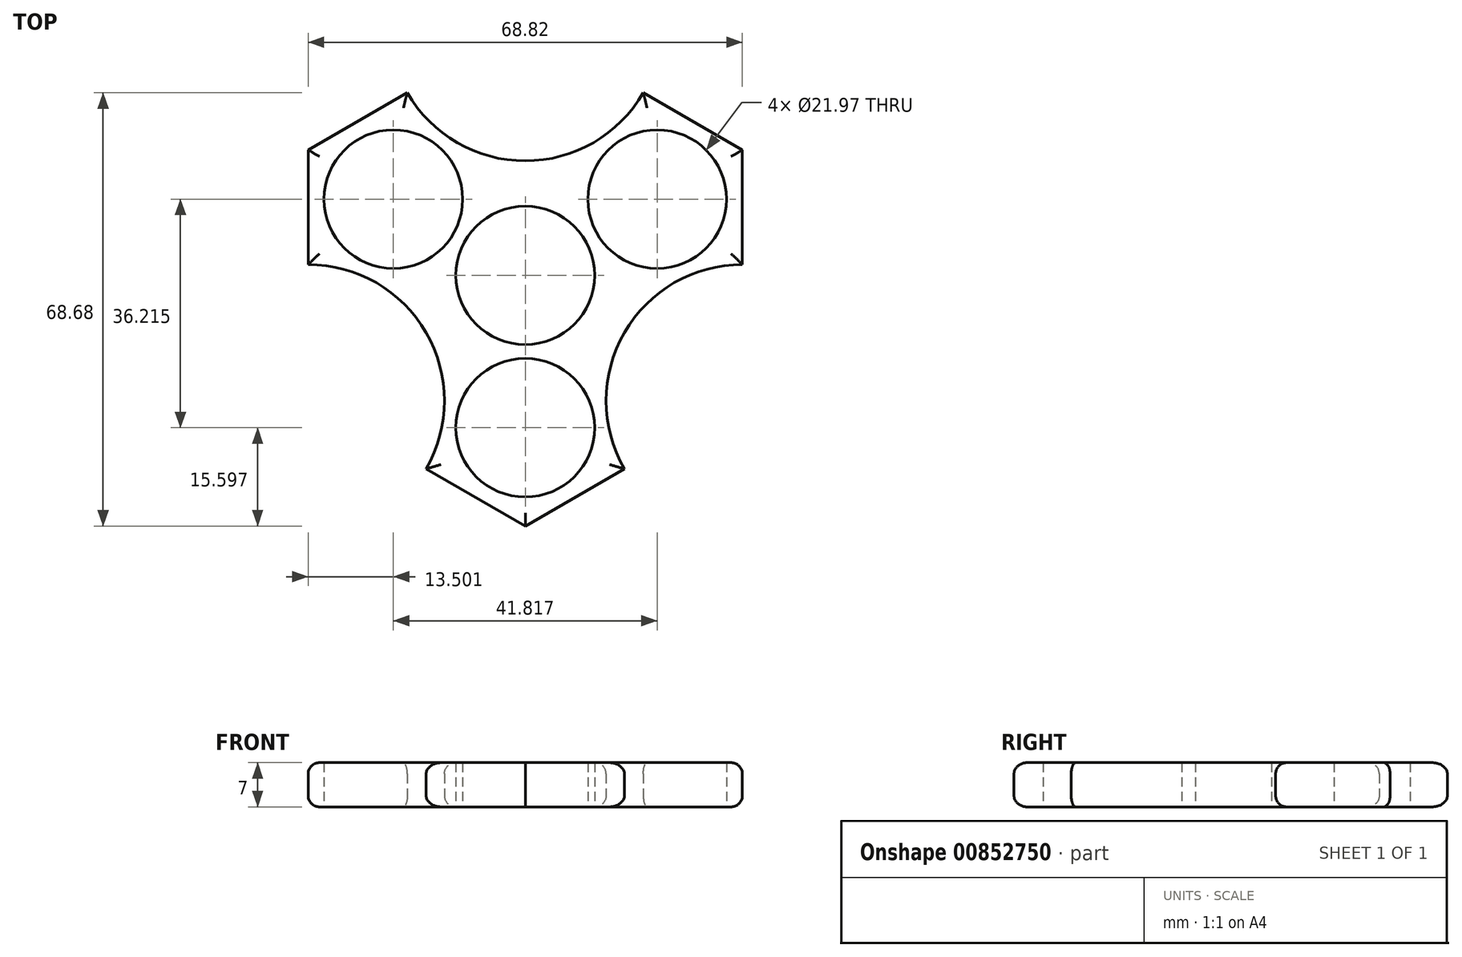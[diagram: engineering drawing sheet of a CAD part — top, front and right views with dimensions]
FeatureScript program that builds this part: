
annotation { "Feature Type Name" : "Feature", "Feature Type Description" : "" }
export const myFeature = defineFeature(function(context is Context, id is Id, definition is map)
    precondition{}
    {
        {
            var Q0;
            Q0=qCreatedBy(makeId("Top.planeOp"),FACE);
            var sketch = newSketch(context, id + "F0", { "sketchPlane" : qUnion([Q0])});
            skCircle(sketch, "E0.cCircle", {"center": v(0, 0) * mm, "radius": 34.41 * mm, "construction": true});
            skLineSegment(sketch, "E0.0", {"start": v(34.41, 19.87) * mm, "end": v(34.41, -19.87) * mm});
            skLineSegment(sketch, "E0.1", {"start": v(34.41, -19.87) * mm, "end": v(0, -39.74) * mm});
            skLineSegment(sketch, "E0.2", {"start": v(0, -39.74) * mm, "end": v(-34.41, -19.87) * mm});
            skLineSegment(sketch, "E0.3", {"start": v(-34.41, -19.87) * mm, "end": v(-34.41, 19.87) * mm});
            skLineSegment(sketch, "E0.4", {"start": v(-34.41, 19.87) * mm, "end": v(0, 39.74) * mm});
            skLineSegment(sketch, "E0.5", {"start": v(0, 39.74) * mm, "end": v(34.41, 19.87) * mm});
            skPoint(sketch, "E0.0.midPoint", {"position": v(34.41, 0) * mm});
            skCircle(sketch, "E1", {"center": v(0, 0) * mm, "radius": 10.99 * mm});
            skCircle(sketch, "E2", {"center": v(0, 39.74) * mm, "radius": 21.59 * mm});
            skCircle(sketch, "E3", {"center": v(34.41, -19.87) * mm, "radius": 21.59 * mm});
            skCircle(sketch, "E4", {"center": v(-34.41, -19.87) * mm, "radius": 21.59 * mm});
            skCircle(sketch, "E5.cCircle", {"center": v(0, 0) * mm, "radius": 20.9 * mm, "construction": true});
            skLineSegment(sketch, "E5.0", {"start": v(20.9, 12.07) * mm, "end": v(20.9, -12.07) * mm, "construction": true});
            skLineSegment(sketch, "E5.1", {"start": v(20.9, -12.07) * mm, "end": v(0, -24.14) * mm, "construction": true});
            skLineSegment(sketch, "E5.2", {"start": v(0, -24.14) * mm, "end": v(-20.9, -12.07) * mm, "construction": true});
            skLineSegment(sketch, "E5.3", {"start": v(-20.9, -12.07) * mm, "end": v(-20.9, 12.07) * mm, "construction": true});
            skLineSegment(sketch, "E5.4", {"start": v(-20.9, 12.07) * mm, "end": v(0, 24.14) * mm, "construction": true});
            skLineSegment(sketch, "E5.5", {"start": v(0, 24.14) * mm, "end": v(20.9, 12.07) * mm, "construction": true});
            skPoint(sketch, "E5.0.midPoint", {"position": v(20.9, 0) * mm});
            skCircle(sketch, "E6", {"center": v(-20.9, 12.07) * mm, "radius": 10.99 * mm});
            skCircle(sketch, "E7", {"center": v(20.9, 12.07) * mm, "radius": 10.99 * mm});
            skCircle(sketch, "E8", {"center": v(0, -24.14) * mm, "radius": 10.99 * mm});
            skSolve(sketch);
        }
        {
            var Q0;
            Q0=makeQuery(id+"F0.imprint","IMPRINT",FACE,{"disambiguationData":[TD([[makeQuery(id+"F0.imprint","IMPRINT",EDGE,{"derivedFrom":sQuery(id+"F0.wireOp",EDGE,"E1")}),-1.0]])]});
            extrude(context, id + "F1", {"entities" : qUnion([Q0]), "depth" : 7 * mm, "offsetDistance" : 25.4 * mm});
        }
        {
            var Q0;
            Q0=makeQuery(id+"F1.opExtrude","CAP_EDGE",EDGE,{"disambiguationData":[OSD([sQuery(id+"F0.wireOp",EDGE,"E4")])],"isStart":false});
            var Q1;
            Q1=makeQuery(id+"F1.opExtrude","CAP_EDGE",EDGE,{"disambiguationData":[OSD([sQuery(id+"F0.wireOp",EDGE,"E0.3")])],"isStart":false});
            var Q2;
            Q2=makeQuery(id+"F1.opExtrude","CAP_EDGE",EDGE,{"disambiguationData":[OSD([sQuery(id+"F0.wireOp",EDGE,"E0.4")])],"isStart":false});
            var Q3;
            Q3=makeQuery(id+"F1.opExtrude","CAP_EDGE",EDGE,{"disambiguationData":[OSD([sQuery(id+"F0.wireOp",EDGE,"E2")])],"isStart":false});
            var Q4;
            Q4=makeQuery(id+"F1.opExtrude","CAP_EDGE",EDGE,{"disambiguationData":[OSD([sQuery(id+"F0.wireOp",EDGE,"E0.5")])],"isStart":false});
            var Q5;
            Q5=makeQuery(id+"F1.opExtrude","CAP_EDGE",EDGE,{"disambiguationData":[OSD([sQuery(id+"F0.wireOp",EDGE,"E0.0")])],"isStart":false});
            var Q6;
            Q6=makeQuery(id+"F1.opExtrude","CAP_EDGE",EDGE,{"disambiguationData":[OSD([sQuery(id+"F0.wireOp",EDGE,"E0.2")])],"isStart":false});
            var Q7;
            Q7=makeQuery(id+"F1.opExtrude","CAP_EDGE",EDGE,{"disambiguationData":[OSD([sQuery(id+"F0.wireOp",EDGE,"E0.1")])],"isStart":false});
            var Q8;
            Q8=makeQuery(id+"F1.opExtrude","CAP_EDGE",EDGE,{"disambiguationData":[OSD([sQuery(id+"F0.wireOp",EDGE,"E3")])],"isStart":false});
            var Q9;
            Q9=makeQuery(id+"F1.opExtrude","CAP_EDGE",EDGE,{"disambiguationData":[OSD([sQuery(id+"F0.wireOp",EDGE,"E3")])],"isStart":true});
            var Q10;
            Q10=makeQuery(id+"F1.opExtrude","CAP_EDGE",EDGE,{"disambiguationData":[OSD([sQuery(id+"F0.wireOp",EDGE,"E0.1")])],"isStart":true});
            var Q11;
            Q11=makeQuery(id+"F1.opExtrude","CAP_EDGE",EDGE,{"disambiguationData":[OSD([sQuery(id+"F0.wireOp",EDGE,"E0.2")])],"isStart":true});
            var Q12;
            Q12=makeQuery(id+"F1.opExtrude","CAP_EDGE",EDGE,{"disambiguationData":[OSD([sQuery(id+"F0.wireOp",EDGE,"E4")])],"isStart":true});
            var Q13;
            Q13=makeQuery(id+"F1.opExtrude","CAP_EDGE",EDGE,{"disambiguationData":[OSD([sQuery(id+"F0.wireOp",EDGE,"E0.3")])],"isStart":true});
            var Q14;
            Q14=makeQuery(id+"F1.opExtrude","CAP_EDGE",EDGE,{"disambiguationData":[OSD([sQuery(id+"F0.wireOp",EDGE,"E0.4")])],"isStart":true});
            var Q15;
            Q15=makeQuery(id+"F1.opExtrude","CAP_EDGE",EDGE,{"disambiguationData":[OSD([sQuery(id+"F0.wireOp",EDGE,"E2")])],"isStart":true});
            var Q16;
            Q16=makeQuery(id+"F1.opExtrude","CAP_EDGE",EDGE,{"disambiguationData":[OSD([sQuery(id+"F0.wireOp",EDGE,"E0.5")])],"isStart":true});
            var Q17;
            Q17=makeQuery(id+"F1.opExtrude","CAP_EDGE",EDGE,{"disambiguationData":[OSD([sQuery(id+"F0.wireOp",EDGE,"E0.0")])],"isStart":true});
            fillet(context, id + "F2", {"entities" : qUnion([Q0, Q1, Q2, Q3, Q4, Q5, Q6, Q7, Q8, Q9, Q10, Q11, Q12, Q13, Q14, Q15, Q16, Q17]), "radius" : 1.78 * mm, "tangentPropagation" : true, "allowEdgeOverflow" : false});
        }
    });
